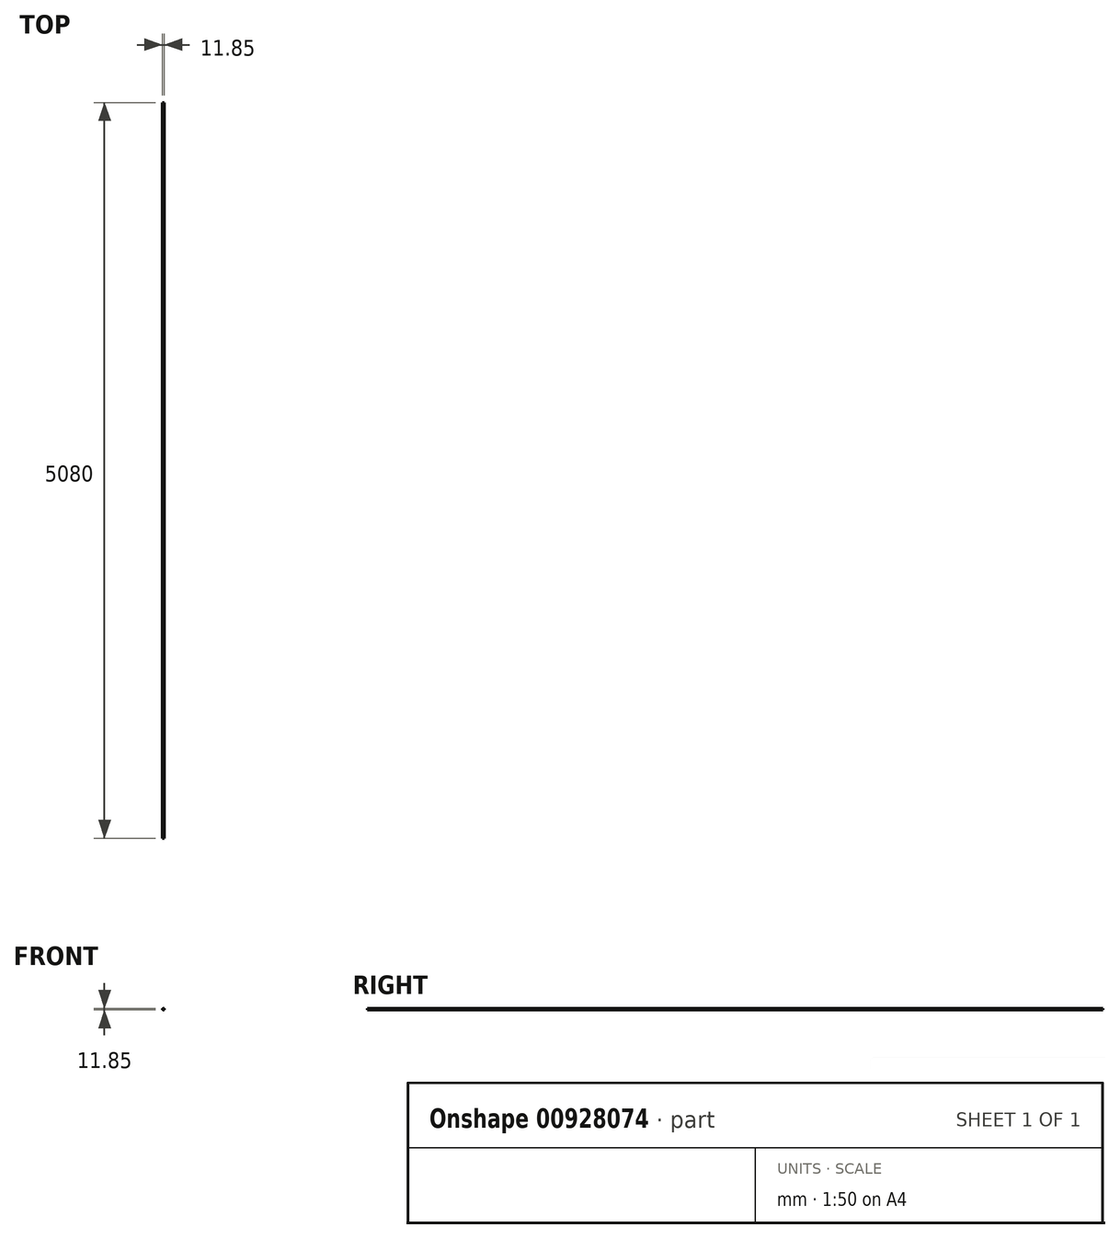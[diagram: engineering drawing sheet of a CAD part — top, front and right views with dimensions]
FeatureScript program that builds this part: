
annotation { "Feature Type Name" : "Feature", "Feature Type Description" : "" }
export const myFeature = defineFeature(function(context is Context, id is Id, definition is map)
    precondition{}
    {
        {
            var Q0;
            Q0=qCreatedBy(makeId("Front.planeOp"),FACE);
            var sketch = newSketch(context, id + "F0", { "sketchPlane" : qUnion([Q0])});
            skCircle(sketch, "E0", {"center": v(-34.22, 24.95) * mm, "radius": 5.92 * mm});
            skSolve(sketch);
        }
        {
            var Q0;
            Q0=sQuery(id+"F0.wireOp",EDGE,"E0");
            extrude(context, id + "F1", {"bodyType" : ToolBodyType.SURFACE, "surfaceEntities" : qUnion([Q0]), "depth" : 2540 * mm, "offsetDistance" : 25.4 * mm, "hasSecondDirection" : true, "secondDirectionOppositeDirection" : true, "secondDirectionDepth" : 2540 * mm});
        }
        {
            var Q0;
            Q0=qCreatedBy(makeId("Front.planeOp"),FACE);
            var sketch = newSketch(context, id + "F2", { "sketchPlane" : qUnion([Q0])});
            skLineSegment(sketch, "E1", {"start": v(-570.8, 345.26) * mm, "end": v(365.53, 116.92) * mm});
            skSolve(sketch);
        }
        {
            var Q0;
            Q0=sQuery(id+"F2.wireOp",EDGE,"E1");
            extrude(context, id + "F3", {"bodyType" : ToolBodyType.SURFACE, "surfaceEntities" : qUnion([Q0]), "depth" : 25.4 * mm, "offsetDistance" : 25.4 * mm});
        }
        {
            var Q0;
            Q0=makeQuery(id+"F3.opExtrude","SWEPT_BODY",BODY,{"disambiguationData":[OSD([sQuery(id+"F2.wireOp",EDGE,"E1")])]});
            deleteBodies(context, id + "F4", {"entities" : qUnion([Q0])});
        }
    });
